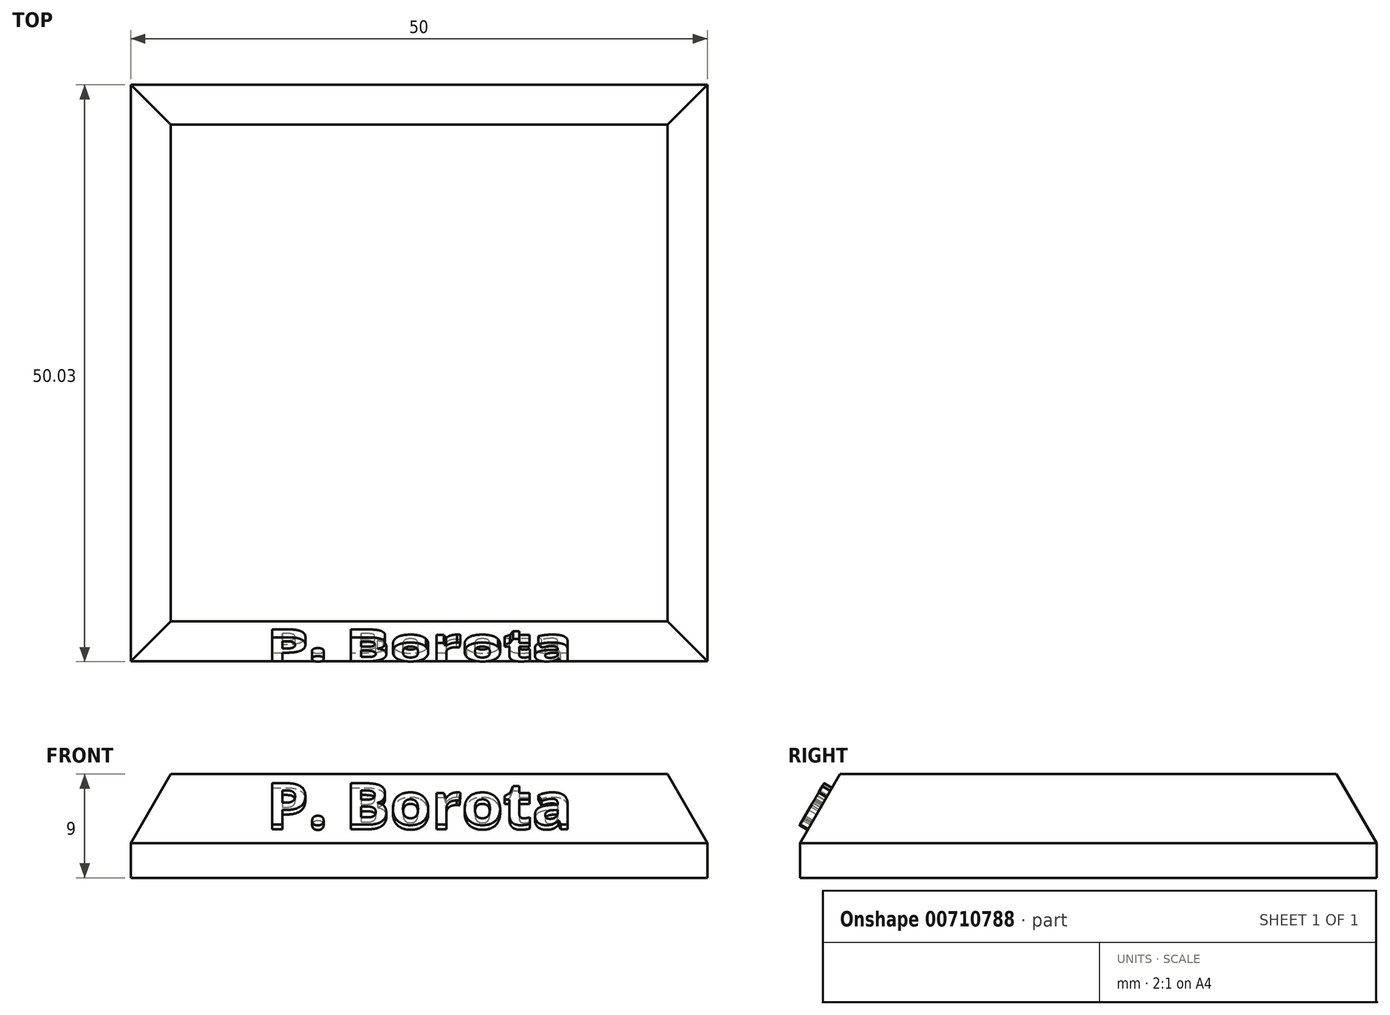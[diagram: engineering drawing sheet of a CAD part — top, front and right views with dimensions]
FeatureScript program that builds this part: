
annotation { "Feature Type Name" : "Feature", "Feature Type Description" : "" }
export const myFeature = defineFeature(function(context is Context, id is Id, definition is map)
    precondition{}
    {
        {
            var Q0;
            Q0=qCreatedBy(makeId("Top.planeOp"),FACE);
            var sketch = newSketch(context, id + "F0", { "sketchPlane" : qUnion([Q0])});
            skLineSegment(sketch, "E0.bottom", {"start": v(-25, 25) * mm, "end": v(25, 25) * mm});
            skLineSegment(sketch, "E0.top", {"start": v(-25, -25) * mm, "end": v(25, -25) * mm});
            skLineSegment(sketch, "E0.left", {"start": v(-25, 25) * mm, "end": v(-25, -25) * mm});
            skLineSegment(sketch, "E0.right", {"start": v(25, 25) * mm, "end": v(25, -25) * mm});
            skPoint(sketch, "E0.middle", {"position": v(0, 0) * mm});
            skSolve(sketch);
        }
        {
            var Q0;
            Q0=makeQuery(id+"F0.imprint","IMPRINT",FACE,{"disambiguationData":[TD([[makeQuery(id+"F0.imprint","IMPRINT",EDGE,{"derivedFrom":sQuery(id+"F0.wireOp",EDGE,"E0.bottom")}),-1.0]])]});
            extrude(context, id + "F1", {"entities" : qUnion([Q0]), "depth" : 9 * mm, "offsetDistance" : 25 * mm});
        }
        {
            var Q0;
            Q0=makeQuery(id+"F1.opExtrude","CAP_FACE",FACE,{"disambiguationData":[OSD([sQuery(id+"F0.wireOp",EDGE,"E0.bottom"),sQuery(id+"F0.wireOp",EDGE,"E0.top"),sQuery(id+"F0.wireOp",EDGE,"E0.left"),sQuery(id+"F0.wireOp",EDGE,"E0.right")])],"isStart":false});
            chamfer(context, id + "F2", {"entities" : qUnion([Q0]), "chamferType" : ChamferType.OFFSET_ANGLE, "width" : 6 * mm, "oppositeDirection" : false, "angle" : 30 * degree, "tangentPropagation" : true});
        }
        {
            var Q0;
            Q0=makeQuery(id+"F2.opChamfer","BLEND_FACE",FACE,{"disambiguationData":[OSD([sQuery(id+"F0.wireOp",EDGE,"E0.top")])]});
            var sketch = newSketch(context, id + "F3", { "sketchPlane" : qUnion([Q0])});
            skText(sketch, "E1", { "text": "P. Borota", "fontName": "OpenSans-Bold.ttf"});
            const initialGuessF3  = {"E1": [-0.01325, -0.0085, 1, 0, 0.00418]};
            skSetInitialGuess(sketch, initialGuessF3);
            skSolve(sketch);
        }
        {
            var Q0;
            Q0 = qSketchRegion(id + "F3", true);
            extrude(context, id + "F4", {"entities" : qUnion([Q0]), "operationType" : NewBodyOperationType.ADD, "depth" : 0.8 * mm, "offsetDistance" : 25 * mm});
        }
    });
